# Revit family: Haworth_XSeries_Locker_Double
name_source: partatom
category: Furniture Systems
revit_build: Autodesk Revit 2018 (Build: 20170223_1515(x64)
units: mm (PartAtom-declared; Revit-internal decimal feet)

## family parameters
Always vertical = Yes
Cut with Voids When Loaded = No
OmniClass Number = 23.40.70.14.64.21
OmniClass Title = Systems Furniture
Part Type = Normal
Room Calculation Point = No
Round Connector Dimension = Use Diameter
Shared = No
Work Plane-Based = No

## types (8) — shared parameters
Actual Height = 51 1/2"
Actual Width = 24"
Assembly Code = E2020200
Base Height = 1 7/8"
Classic Pull = No
Crescent Pull = No
Custom Depth = No
Custom Height = No
Custom Size = No
Custom Width = No
Description = Haworth XSeries Locker - Double
Door Height = 48 1/4"
Door Offset = 1/16"
Door Width = 11 7/8"
Height = 51 1/2"
J Pull = No
Linear Pull = Yes
Manufacturer = Haworth
Max. Depth = 23 3/4"
Max. Height = 64 1/2"
Max. Width = 24"
Min. Depth = 18 3/4"
Min. Height = 39 1/2"
Min. Width = 24"
Model = JA18-5124
Panel Thickness = 3/4"
Pull Ellipse = No
Pull Finish = Haworth _ Metal _ Brushed Aluminum
Pull Height = 24 1/8"
Pull Offset Centerline = 10 1/2"
Radius Pull = No
Revision Number = 3
Size = Verify Final Dim. w/ Haworth
Standard Depths = 18.75, 23.75 in.
Standard Heights = 39.5, 40.5, 48.5, 51.5, 56.5, 63.5, 64.5 in.
Standard Widths = 24 in.
Sustainability Info = https://www.haworth.com
Taper Pull = No
Top Height = 1 1/4"
URL = http://www.haworth.com
URL - Product = https://www.haworth.com
Warranty = http://www.haworth.com
Width = 24"

## per-type parameters (varying)
| type | Actual Depth | Center Hinged | Depth | Door Left Inside | Door Left Outside | Door Right Inside | Door Right Outside | Left Hand | Outside Hinged | Right Hand |
| 18d 24w 51h - Right Hand | 18 3/4" | No | 18 3/4" | Yes | No | No | Yes | No | No | Yes |
| 18d 24w 51h - Left Hand | 18 3/4" | No | 18 3/4" | No | Yes | Yes | No | Yes | No | No |
| 18d 24w 51h - Center Hinged | 18 3/4" | Yes | 18 3/4" | Yes | No | Yes | No | No | No | No |
| 18d 24w 51h - Outside Hinged | 18 3/4" | No | 18 3/4" | No | Yes | No | Yes | No | Yes | No |
| 24d 24w 51h - Center Hinged | 23 3/4" | Yes | 23 3/4" | Yes | No | Yes | No | No | No | No |
| 24d 24w 51h - Left Hand | 23 3/4" | No | 23 3/4" | No | Yes | Yes | No | Yes | No | No |
| 24d 24w 51h - Outside Hinged | 23 3/4" | No | 23 3/4" | No | Yes | No | Yes | No | Yes | No |
| 24d 24w 51h - Right Hand | 23 3/4" | No | 23 3/4" | Yes | No | No | Yes | No | No | Yes |

## geometry (parser evidence)
native form markers: Sweep x9
no freeform markers — native parametric forms only
